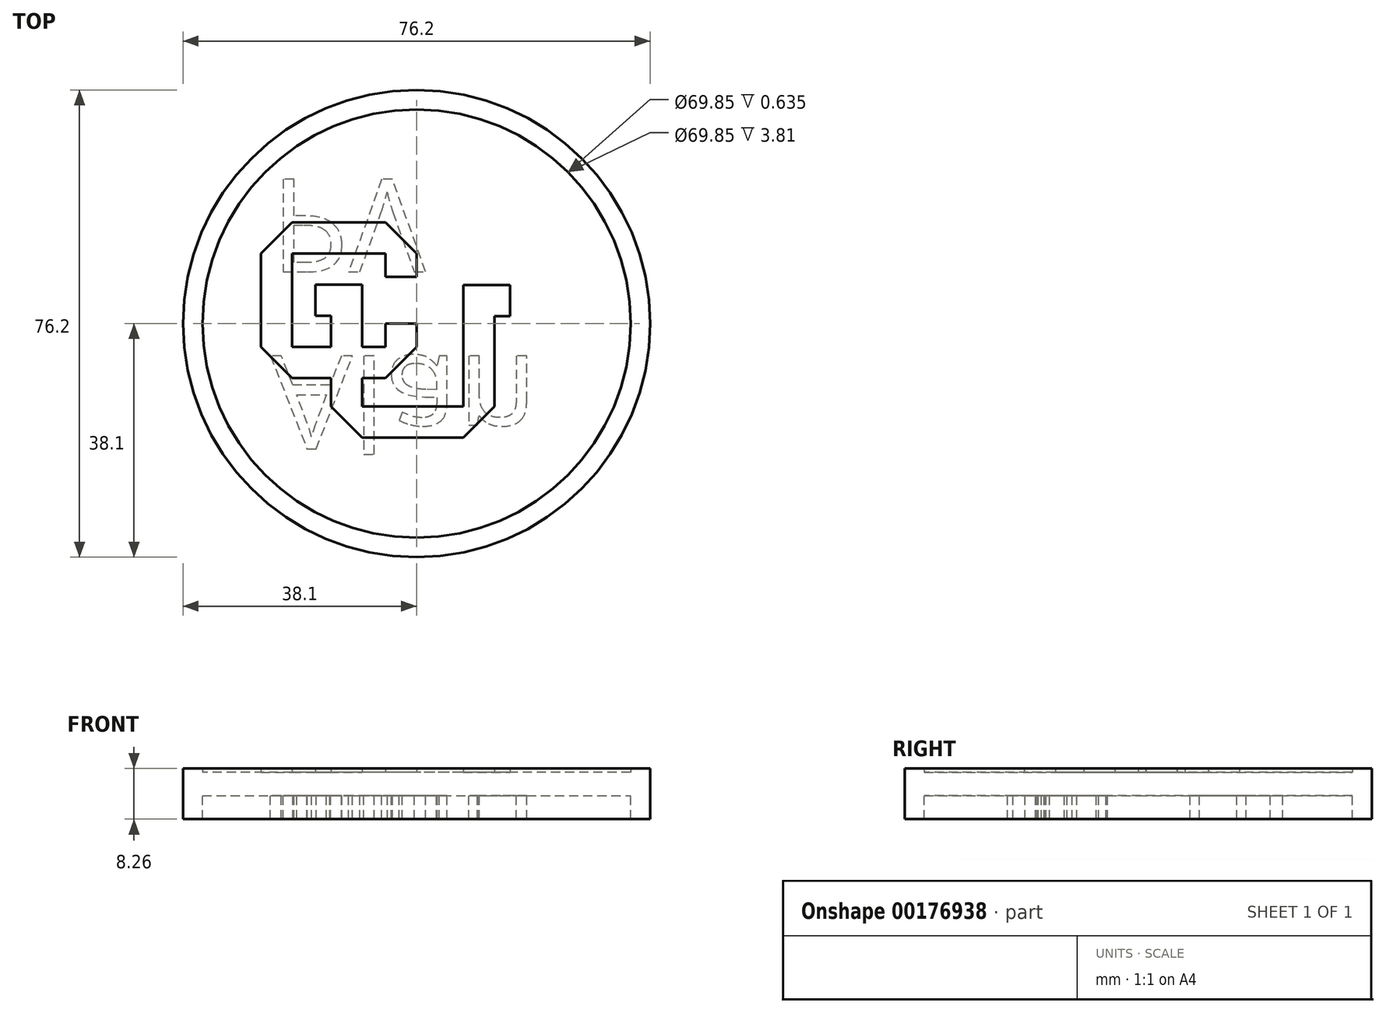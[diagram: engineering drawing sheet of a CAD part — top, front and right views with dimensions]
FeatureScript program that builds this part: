
annotation { "Feature Type Name" : "Feature", "Feature Type Description" : "" }
export const myFeature = defineFeature(function(context is Context, id is Id, definition is map)
    precondition{}
    {
        {
            var Q0;
            Q0=qCreatedBy(makeId("Top.planeOp"),FACE);
            var sketch = newSketch(context, id + "F0", { "sketchPlane" : qUnion([Q0])});
            skCircle(sketch, "E0", {"center": v(0, 0) * mm, "radius": 38.1 * mm});
            skSolve(sketch);
        }
        {
            var Q0;
            Q0=makeQuery(id+"F0.imprint","IMPRINT",FACE,{"disambiguationData":[TD([[makeQuery(id+"F0.imprint","IMPRINT",EDGE,{"derivedFrom":sQuery(id+"F0.wireOp",EDGE,"E0")}),1.0]])]});
            var Q1;
            Q1 = qConstructionFilter(qBodyType(qCreatedBy(id + "F0" ,EDGE), BodyType.WIRE), ConstructionObject.NO);
            extrude(context, id + "F1", {"entities" : qUnion([Q0]), "surfaceEntities" : qUnion([Q1]), "depth" : 3.8 * mm});
        }
        {
            var Q0;
            Q0=qCreatedBy(makeId("Top.planeOp"),FACE);
            var sketch = newSketch(context, id + "F2", { "sketchPlane" : qUnion([Q0])});
            skLineSegment(sketch, "E1", {"start": v(0, 0) * mm, "end": v(0, -3.81) * mm});
            skLineSegment(sketch, "E2", {"start": v(0, -3.81) * mm, "end": v(-5.08, -8.9) * mm});
            skLineSegment(sketch, "E3", {"start": v(-20.32, -8.9) * mm, "end": v(-25.4, -3.81) * mm});
            skLineSegment(sketch, "E4", {"start": v(-25.4, -3.81) * mm, "end": v(-25.4, 11.43) * mm});
            skLineSegment(sketch, "E5", {"start": v(-25.4, 11.43) * mm, "end": v(-20.32, 16.5) * mm});
            skLineSegment(sketch, "E6", {"start": v(-20.32, 16.5) * mm, "end": v(-5.08, 16.5) * mm});
            skLineSegment(sketch, "E7", {"start": v(-5.08, 16.51) * mm, "end": v(0, 11.43) * mm});
            skLineSegment(sketch, "E8", {"start": v(0, 11.43) * mm, "end": v(0, 7.62) * mm});
            skLineSegment(sketch, "E9", {"start": v(0, 7.62) * mm, "end": v(-5.08, 7.62) * mm});
            skLineSegment(sketch, "E10", {"start": v(-5.08, 7.62) * mm, "end": v(-5.08, 11.43) * mm});
            skLineSegment(sketch, "E11", {"start": v(-5.08, 11.43) * mm, "end": v(-20.32, 11.43) * mm});
            skLineSegment(sketch, "E12", {"start": v(-20.32, 11.43) * mm, "end": v(-20.32, -3.81) * mm});
            skLineSegment(sketch, "E13", {"start": v(-5.08, -3.81) * mm, "end": v(-5.08, 0) * mm});
            skLineSegment(sketch, "E14", {"start": v(-5.08, 0) * mm, "end": v(0, 0) * mm});
            skLineSegment(sketch, "E15", {"start": v(-8.9, 6.35) * mm, "end": v(-16.51, 6.35) * mm});
            skLineSegment(sketch, "E16", {"start": v(-16.51, 6.35) * mm, "end": v(-16.51, 1.27) * mm});
            skLineSegment(sketch, "E17", {"start": v(-8.9, 6.35) * mm, "end": v(-8.9, -3.81) * mm});
            skLineSegment(sketch, "E18.trimOffspring", {"start": v(-8.9, -3.81) * mm, "end": v(-5.08, -3.81) * mm});
            skLineSegment(sketch, "E19", {"start": v(-8.9, -18.6) * mm, "end": v(7.62, -18.6) * mm});
            skLineSegment(sketch, "E20", {"start": v(7.62, -18.6) * mm, "end": v(12.7, -13.52) * mm});
            skLineSegment(sketch, "E21", {"start": v(12.7, -13.52) * mm, "end": v(12.7, 1.21) * mm});
            skLineSegment(sketch, "E22", {"start": v(12.7, 1.21) * mm, "end": v(15.24, 1.21) * mm});
            skLineSegment(sketch, "E23", {"start": v(15.24, 1.21) * mm, "end": v(15.24, 6.3) * mm});
            skLineSegment(sketch, "E24", {"start": v(15.24, 6.3) * mm, "end": v(7.62, 6.3) * mm});
            skLineSegment(sketch, "E25", {"start": v(7.62, 6.3) * mm, "end": v(7.62, -13.52) * mm});
            skLineSegment(sketch, "E26", {"start": v(-13.97, -3.81) * mm, "end": v(-13.97, 1.27) * mm});
            skLineSegment(sketch, "E27", {"start": v(-13.97, 1.27) * mm, "end": v(-16.51, 1.27) * mm});
            skLineSegment(sketch, "E28", {"start": v(-13.97, -3.81) * mm, "end": v(-20.32, -3.81) * mm});
            skLineSegment(sketch, "E29", {"start": v(-13.97, -8.9) * mm, "end": v(-13.97, -13.52) * mm});
            skLineSegment(sketch, "E30", {"start": v(-13.97, -13.52) * mm, "end": v(-8.9, -18.6) * mm});
            skLineSegment(sketch, "E31", {"start": v(-5.08, -8.9) * mm, "end": v(-8.9, -8.9) * mm});
            skLineSegment(sketch, "E32", {"start": v(-13.97, -8.9) * mm, "end": v(-20.32, -8.9) * mm});
            skPoint(sketch, "E33.end.orphan", {"position": v(-8.9, -13.45) * mm});
            skLineSegment(sketch, "E34", {"start": v(-8.9, -8.9) * mm, "end": v(-8.9, -13.52) * mm});
            skLineSegment(sketch, "E35", {"start": v(-8.9, -13.52) * mm, "end": v(7.62, -13.52) * mm});
            skSolve(sketch);
        }
        {
            var Q0;
            Q0=qCreatedBy(makeId("Top.planeOp"),FACE);
            var sketch = newSketch(context, id + "F3", { "sketchPlane" : qUnion([Q0])});
            skCircle(sketch, "E36", {"center": v(0, 0) * mm, "radius": 34.93 * mm});
            skCircle(sketch, "E37", {"center": v(0, 0) * mm, "radius": 38.1 * mm});
            skSolve(sketch);
        }
        {
            var Q0;
            Q0 = qSketchRegion(id + "F3", true);
            var Q1;
            Q1 = qSketchRegion(id + "F2", true);
            extrude(context, id + "F4", {"entities" : qUnion([Q0, Q1]), "operationType" : NewBodyOperationType.ADD, "depth" : 4.44 * mm});
        }
        {
            var Q0;
            Q0=makeQuery(id+"F1.opExtrude","CAP_FACE",FACE,{"disambiguationData":[OSD([sQuery(id+"F0.wireOp",EDGE,"E0")])],"isStart":true});
            var sketch = newSketch(context, id + "F5", { "sketchPlane" : qUnion([Q0])});
            skCircle(sketch, "E38", {"center": v(0, 0) * mm, "radius": 34.93 * mm});
            skSolve(sketch);
        }
        {
            var Q0;
            Q0=makeQuery(id+"F5.imprint","IMPRINT",FACE,{"disambiguationData":[TD([[makeQuery(id+"F5.imprint","IMPRINT",EDGE,{"derivedFrom":sQuery(id+"F5.wireOp",EDGE,"E38")}),1.0]])]});
            var sketch = newSketch(context, id + "F6", { "sketchPlane" : qUnion([Q0])});
            skText(sketch, "E39", { "text": "Alan \nPV", "fontName": "OpenSans-Regular.ttf"});
            const initialGuessF6  = {"E39": [-0.02384, 0.00525, 1, 0, 0.01524]};
            skSetInitialGuess(sketch, initialGuessF6);
            skSolve(sketch);
        }
        {
            var Q0;
            Q0 = qSketchRegion(id + "F6", true);
            var Q1;
            Q1=makeQuery(id+"F5.imprint","IMPRINT",FACE,{"disambiguationData":[TD([[makeQuery(id+"F5.imprint","IMPRINT",EDGE,{"derivedFrom":sQuery(id+"F5.wireOp",EDGE,"E38")}),-1.0]])]});
            extrude(context, id + "F7", {"entities" : qUnion([Q0, Q1]), "operationType" : NewBodyOperationType.ADD, "depth" : 3.8 * mm});
        }
    });
